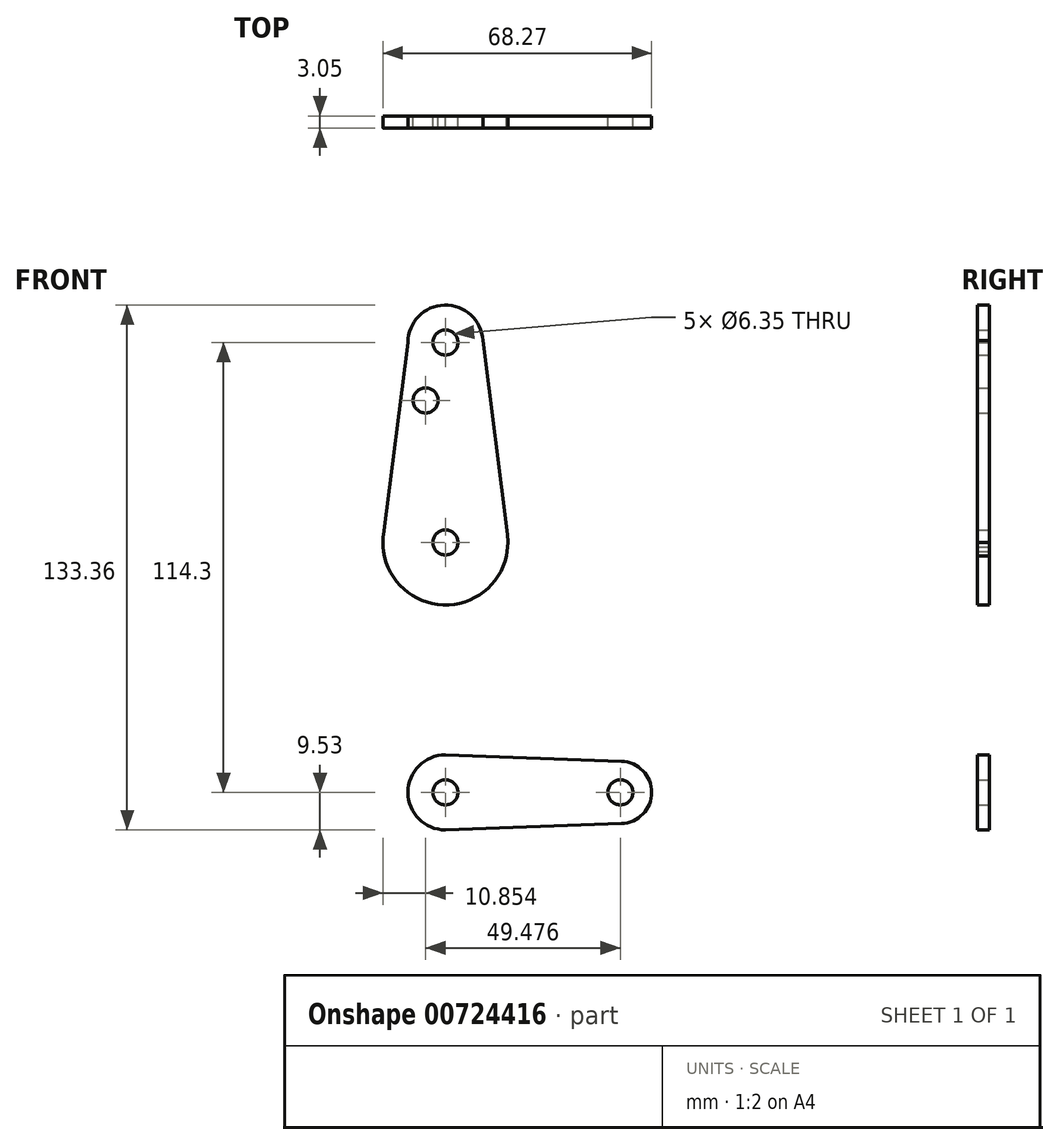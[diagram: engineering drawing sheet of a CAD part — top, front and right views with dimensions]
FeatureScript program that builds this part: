
annotation { "Feature Type Name" : "Feature", "Feature Type Description" : "" }
export const myFeature = defineFeature(function(context is Context, id is Id, definition is map)
    precondition{}
    {
        {
            var Q0;
            Q0=qCreatedBy(makeId("Front.planeOp"),FACE);
            var sketch = newSketch(context, id + "F0", { "sketchPlane" : qUnion([Q0])});
            skLineSegment(sketch, "E0", {"start": v(0, 114.3) * mm, "end": v(0, 0) * mm, "construction": true});
            skLineSegment(sketch, "E1", {"start": v(0, 0) * mm, "end": v(44.45, 0) * mm, "construction": true});
            skCircle(sketch, "E2", {"center": v(0, 114.3) * mm, "radius": 9.53 * mm});
            skCircle(sketch, "E3", {"center": v(0, 63.5) * mm, "radius": 15.88 * mm});
            skCircle(sketch, "E4", {"center": v(0, 0) * mm, "radius": 9.53 * mm});
            skCircle(sketch, "E5", {"center": v(44.45, 0) * mm, "radius": 7.94 * mm});
            skLineSegment(sketch, "E6", {"start": v(0, -9.53) * mm, "end": v(44.73, -7.93) * mm});
            skLineSegment(sketch, "E7", {"start": v(0, 9.53) * mm, "end": v(44.73, 7.93) * mm});
            skLineSegment(sketch, "E8", {"start": v(-9.52, 114.32) * mm, "end": v(-15.75, 65.5) * mm});
            skLineSegment(sketch, "E9", {"start": v(9.51, 114.83) * mm, "end": v(15.75, 65.5) * mm});
            skLineSegment(sketch, "E10", {"start": v(-15.83, 62.3) * mm, "end": v(-9.15, 2.66) * mm});
            skLineSegment(sketch, "E11", {"start": v(15.88, 63.5) * mm, "end": v(9.22, 2.4) * mm});
            skCircle(sketch, "E12", {"center": v(0, 63.5) * mm, "radius": 3.18 * mm});
            skCircle(sketch, "E13", {"center": v(0, 114.3) * mm, "radius": 3.18 * mm});
            skCircle(sketch, "E14", {"center": v(0, 0) * mm, "radius": 3.18 * mm});
            skCircle(sketch, "E15", {"center": v(44.45, 0) * mm, "radius": 3.18 * mm});
            skCircle(sketch, "E16", {"center": v(-5.03, 99.6) * mm, "radius": 3.18 * mm});
            skSolve(sketch);
        }
        {
            var Q0;
            {var subQ1=sQuery(id+"F0.wireOp",EDGE,"E8");Q0=makeQuery(id+"F0.imprint","IMPRINT",FACE,{"disambiguationData":[TD([[makeQuery(id+"F0.imprint","IMPRINT",EDGE,{"derivedFrom":subQ1}),1.0]])]});}
            var Q1;
            Q1=makeQuery(id+"F0.imprint","IMPRINT",FACE,{"disambiguationData":[TD([[makeQuery(id+"F0.imprint","IMPRINT",EDGE,{"derivedFrom":sQuery(id+"F0.wireOp",EDGE,"E12")}),-1.0]])]});
            var Q2;
            {var subQ3=sQuery(id+"F0.wireOp",EDGE,"E10");var subQ8=sQuery(id+"F0.wireOp",EDGE,"E3");var subQ9=makeQuery(id+"F0.imprint","INTERSECT",VERTEX,{"disambiguationData":[OD(1.0)],"derivedFrom":[subQ8,subQ3]});Q2=makeQuery(id+"F0.imprint","IMPRINT",FACE,{"disambiguationData":[TD([[makeQuery(id+"F0.imprint","IMPRINT",EDGE,{"disambiguationData":[TD([[subQ9,-1.0]])],"derivedFrom":subQ8}),-1.0]])]});}
            var Q3;
            Q3=makeQuery(id+"F0.imprint","IMPRINT",FACE,{"disambiguationData":[TD([[makeQuery(id+"F0.imprint","IMPRINT",EDGE,{"derivedFrom":sQuery(id+"F0.wireOp",EDGE,"E14")}),-1.0]])]});
            var Q4;
            {var subQ3=sQuery(id+"F0.wireOp",EDGE,"E11");var subQ7=sQuery(id+"F0.wireOp",EDGE,"E4");var subQ9=makeQuery(id+"F0.imprint","INTERSECT",VERTEX,{"derivedFrom":[subQ7,subQ3]});Q4=makeQuery(id+"F0.imprint","IMPRINT",FACE,{"disambiguationData":[TD([[makeQuery(id+"F0.imprint","IMPRINT",EDGE,{"disambiguationData":[TD([[subQ9,1.0]])],"derivedFrom":subQ7}),-1.0]])]});}
            var Q5;
            {var subQ0=sQuery(id+"F0.wireOp",EDGE,"E11");var subQ1=sQuery(id+"F0.wireOp",EDGE,"E4");var subQ2=makeQuery(id+"F0.imprint","INTERSECT",VERTEX,{"derivedFrom":[subQ1,subQ0]});Q5=makeQuery(id+"F0.imprint","IMPRINT",FACE,{"disambiguationData":[TD([[makeQuery(id+"F0.imprint","IMPRINT",EDGE,{"disambiguationData":[TD([[subQ2,-1.0]])],"derivedFrom":subQ1}),-1.0]])]});}
            var Q6;
            Q6=makeQuery(id+"F0.imprint","IMPRINT",FACE,{"disambiguationData":[TD([[makeQuery(id+"F0.imprint","IMPRINT",EDGE,{"derivedFrom":sQuery(id+"F0.wireOp",EDGE,"E15")}),-1.0]])]});
            var Q7;
            Q7=makeQuery(id+"F0.imprint","IMPRINT",FACE,{"disambiguationData":[TD([[makeQuery(id+"F0.imprint","IMPRINT",EDGE,{"derivedFrom":sQuery(id+"F0.wireOp",EDGE,"E13")}),-1.0]])]});
            extrude(context, id + "F1", {"entities" : qUnion([Q0, Q1, Q2, Q3, Q4, Q5, Q6, Q7]), "depth" : 3.05 * mm, "offsetDistance" : 25.4 * mm});
        }
    });
